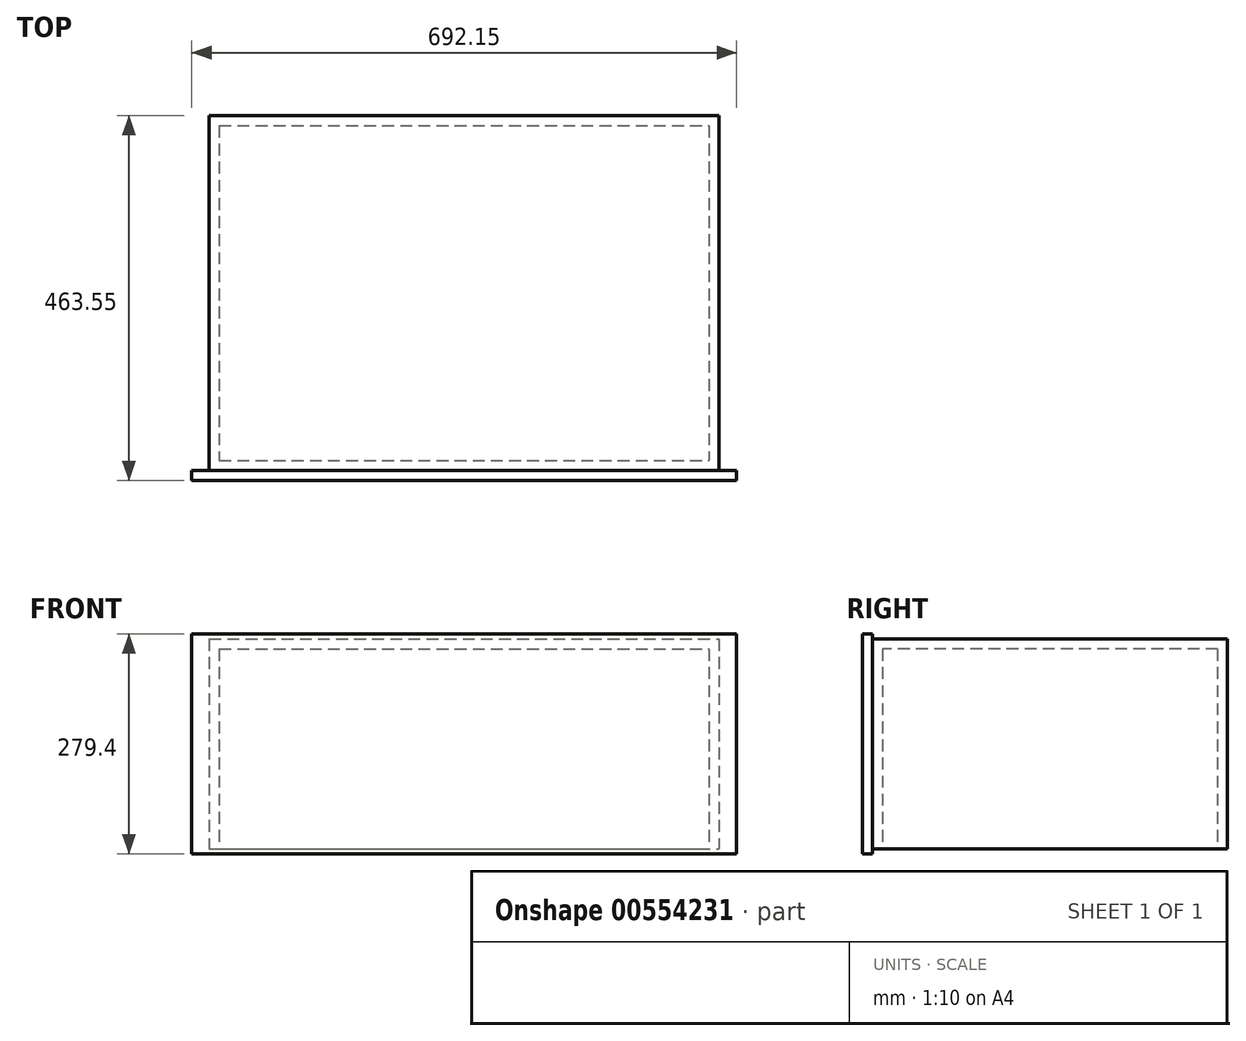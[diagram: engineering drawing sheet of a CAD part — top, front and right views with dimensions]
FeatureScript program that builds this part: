
annotation { "Feature Type Name" : "Feature", "Feature Type Description" : "" }
export const myFeature = defineFeature(function(context is Context, id is Id, definition is map)
    precondition{}
    {
        {
            var Q0;
            Q0=qCreatedBy(makeId("Top.planeOp"),FACE);
            var sketch = newSketch(context, id + "F0", { "sketchPlane" : qUnion([Q0])});
            skLineSegment(sketch, "E0.bottom", {"start": v(-323.73, 253.24) * mm, "end": v(323.97, 253.24) * mm});
            skLineSegment(sketch, "E0.top", {"start": v(-323.73, -197.61) * mm, "end": v(323.97, -197.61) * mm});
            skLineSegment(sketch, "E0.left", {"start": v(-323.73, 253.24) * mm, "end": v(-323.73, -197.61) * mm});
            skLineSegment(sketch, "E0.right", {"start": v(323.97, 253.24) * mm, "end": v(323.97, -197.61) * mm});
            skLineSegment(sketch, "E1.0", {"start": v(-311.03, 240.54) * mm, "end": v(311.27, 240.54) * mm});
            skLineSegment(sketch, "E1.1", {"start": v(-311.03, 240.54) * mm, "end": v(-311.03, -184.91) * mm});
            skLineSegment(sketch, "E1.2", {"start": v(-311.03, -184.91) * mm, "end": v(311.27, -184.91) * mm});
            skLineSegment(sketch, "E1.3", {"start": v(311.27, 240.54) * mm, "end": v(311.27, -184.91) * mm});
            skSolve(sketch);
        }
        {
            var Q0;
            Q0=makeQuery(id+"F0.imprint","IMPRINT",FACE,{"disambiguationData":[TD([[makeQuery(id+"F0.imprint","IMPRINT",EDGE,{"derivedFrom":sQuery(id+"F0.wireOp",EDGE,"E0.bottom")}),-1.0]])]});
            extrude(context, id + "F1", {"entities" : qUnion([Q0]), "depth" : 266.7 * mm, "offsetDistance" : 25.4 * mm});
        }
        {
            var Q0;
            Q0=makeQuery(id+"F1.opExtrude","SWEPT_FACE",FACE,{"disambiguationData":[OSD([sQuery(id+"F0.wireOp",EDGE,"E0.top")])]});
            var sketch = newSketch(context, id + "F2", { "sketchPlane" : qUnion([Q0])});
            skLineSegment(sketch, "E2.bottom", {"start": v(-345.96, 273.05) * mm, "end": v(346.2, 273.05) * mm});
            skLineSegment(sketch, "E2.top", {"start": v(-345.96, -6.35) * mm, "end": v(346.2, -6.35) * mm});
            skLineSegment(sketch, "E2.left", {"start": v(-345.96, 273.05) * mm, "end": v(-345.96, -6.35) * mm});
            skLineSegment(sketch, "E2.right", {"start": v(346.2, 273.05) * mm, "end": v(346.2, -6.35) * mm});
            skPoint(sketch, "E3", {"position": v(-323.73, 266.7) * mm});
            skPoint(sketch, "E4", {"position": v(-323.73, 0) * mm});
            skPoint(sketch, "E5", {"position": v(323.97, 0) * mm});
            skPoint(sketch, "E6", {"position": v(323.97, 266.7) * mm});
            skLineSegment(sketch, "E7", {"start": v(-323.73, 266.7) * mm, "end": v(323.97, 266.7) * mm});
            skLineSegment(sketch, "E8", {"start": v(323.97, 0) * mm, "end": v(323.97, 266.7) * mm});
            skSolve(sketch);
        }
        {
            var Q0;
            Q0 = qSketchRegion(id + "F2", true);
            extrude(context, id + "F3", {"entities" : qUnion([Q0]), "operationType" : NewBodyOperationType.ADD, "depth" : 12.7 * mm, "offsetDistance" : 25.4 * mm});
        }
        {
            var Q0;
            Q0=makeQuery(id+"F1.opExtrude","CAP_FACE",FACE,{"disambiguationData":[OSD([sQuery(id+"F0.wireOp",EDGE,"E0.bottom"),sQuery(id+"F0.wireOp",EDGE,"E0.top"),sQuery(id+"F0.wireOp",EDGE,"E0.left"),sQuery(id+"F0.wireOp",EDGE,"E0.right"),sQuery(id+"F0.wireOp",EDGE,"E1.0"),sQuery(id+"F0.wireOp",EDGE,"E1.1"),sQuery(id+"F0.wireOp",EDGE,"E1.2"),sQuery(id+"F0.wireOp",EDGE,"E1.3")])],"isStart":false});
            var sketch = newSketch(context, id + "F4", { "sketchPlane" : qUnion([Q0])});
            skLineSegment(sketch, "E9", {"start": v(-311.03, 240.54) * mm, "end": v(-311.03, -184.91) * mm});
            skLineSegment(sketch, "E10", {"start": v(-311.03, -184.91) * mm, "end": v(311.27, -184.91) * mm});
            skLineSegment(sketch, "E11", {"start": v(311.27, -184.91) * mm, "end": v(311.27, 240.54) * mm});
            skLineSegment(sketch, "E12", {"start": v(311.27, 240.54) * mm, "end": v(-311.03, 240.54) * mm});
            skSolve(sketch);
        }
        {
            var Q0;
            Q0 = qSketchRegion(id + "F4", true);
            extrude(context, id + "F5", {"entities" : qUnion([Q0]), "operationType" : NewBodyOperationType.ADD, "oppositeDirection" : true, "depth" : 12.7 * mm, "offsetDistance" : 25.4 * mm});
        }
    });
